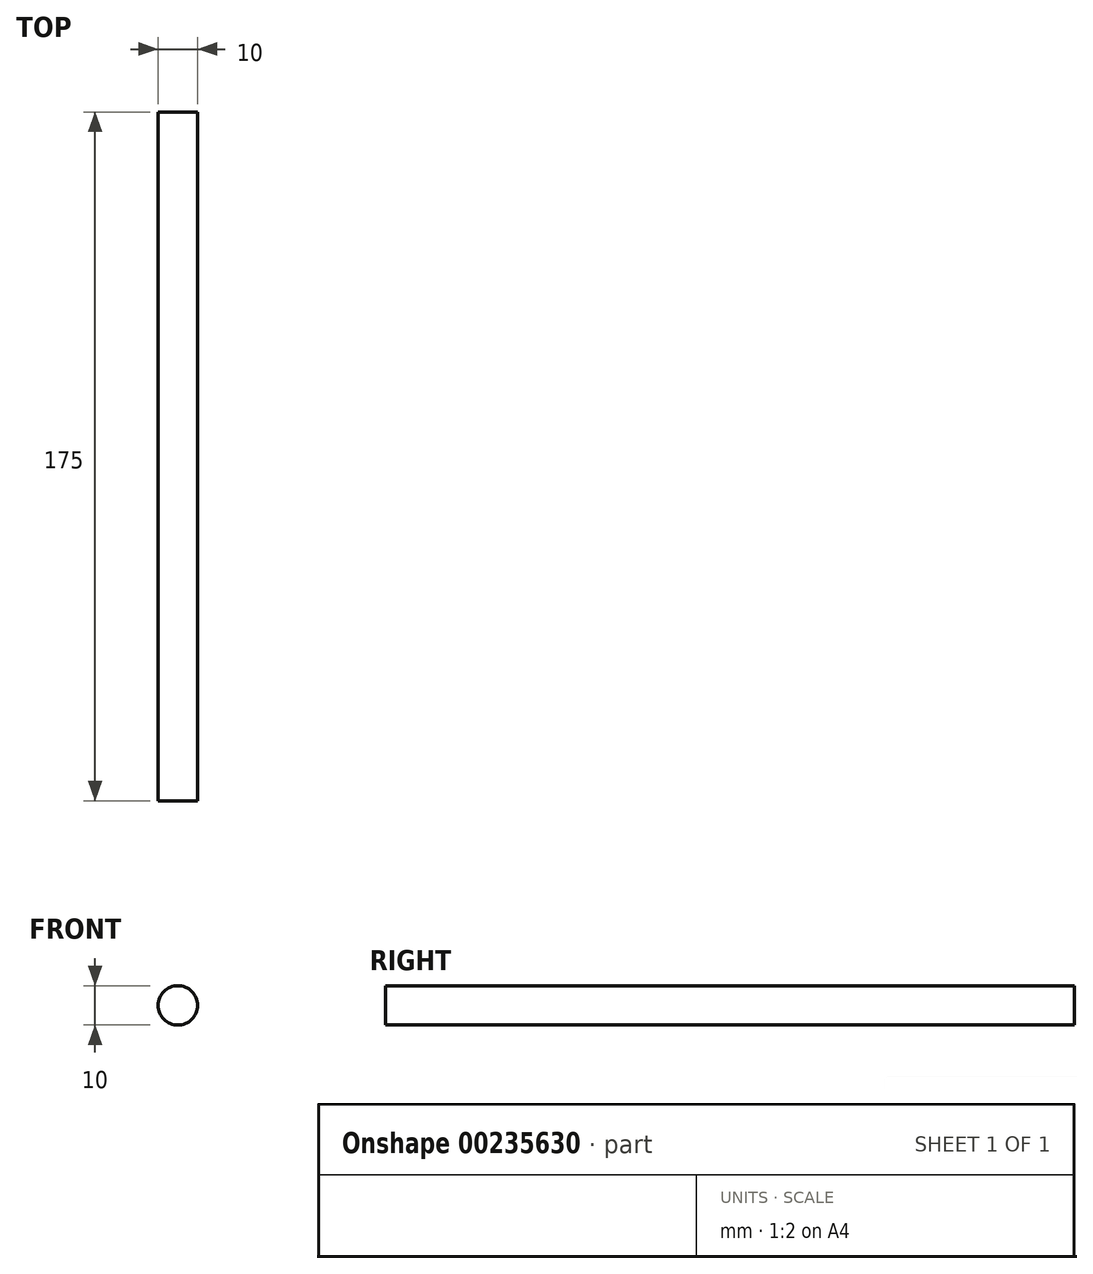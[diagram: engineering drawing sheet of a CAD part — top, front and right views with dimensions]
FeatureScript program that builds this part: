
annotation { "Feature Type Name" : "Feature", "Feature Type Description" : "" }
export const myFeature = defineFeature(function(context is Context, id is Id, definition is map)
    precondition{}
    {
        {
            var Q0;
            Q0=qCreatedBy(makeId("Front.planeOp"),FACE);
            var sketch = newSketch(context, id + "F0", { "sketchPlane" : qUnion([Q0])});
            skCircle(sketch, "E0", {"center": v(0, 0) * mm, "radius": 5 * mm});
            skSolve(sketch);
        }
        {
            var Q0;
            Q0 = qSketchRegion(id + "F0", true);
            extrude(context, id + "F1", {"entities" : qUnion([Q0]), "depth" : 175 * mm});
        }
    });
